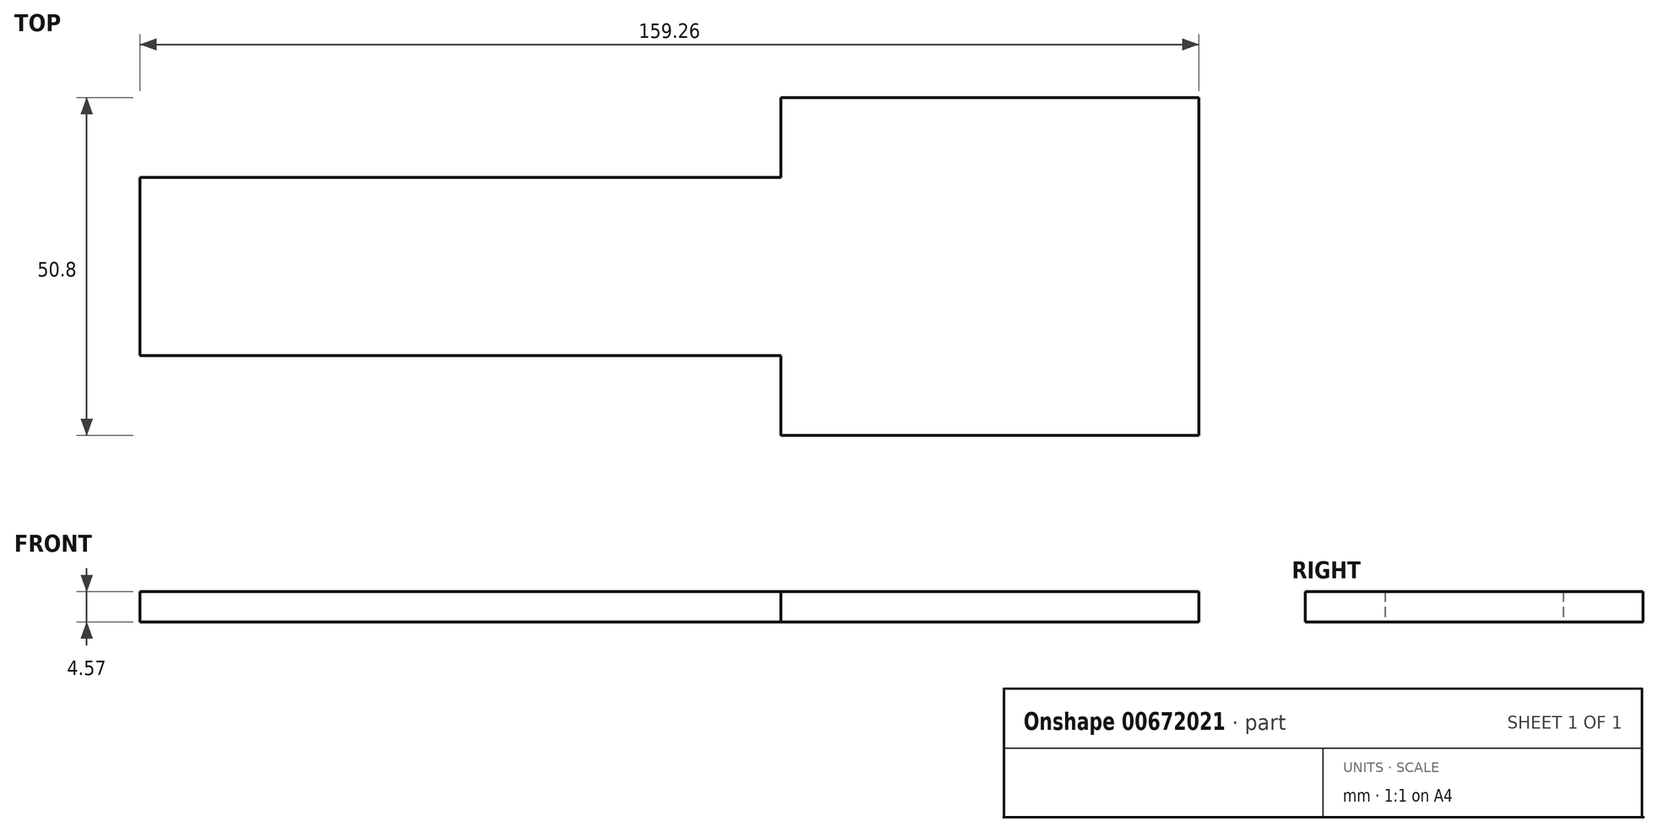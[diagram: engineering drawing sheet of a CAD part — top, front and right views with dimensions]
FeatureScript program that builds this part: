
annotation { "Feature Type Name" : "Feature", "Feature Type Description" : "" }
export const myFeature = defineFeature(function(context is Context, id is Id, definition is map)
    precondition{}
    {
        {
            var Q0;
            Q0=qCreatedBy(makeId("Top.planeOp"),FACE);
            var sketch = newSketch(context, id + "F0", { "sketchPlane" : qUnion([Q0])});
            skLineSegment(sketch, "E0", {"start": v(0, 0) * mm, "end": v(0, 25.4) * mm});
            skLineSegment(sketch, "E1", {"start": v(0, 25.4) * mm, "end": v(-62.87, 25.4) * mm});
            skLineSegment(sketch, "E2", {"start": v(-62.87, 25.4) * mm, "end": v(-62.87, 13.4) * mm});
            skLineSegment(sketch, "E3", {"start": v(-62.87, 13.4) * mm, "end": v(-159.26, 13.4) * mm});
            skLineSegment(sketch, "E4", {"start": v(-159.26, 13.4) * mm, "end": v(-159.26, 0) * mm});
            skLineSegment(sketch, "E5", {"start": v(-159.26, 0) * mm, "end": v(0, 0) * mm});
            skPoint(sketch, "E6", {"position": v(-73, 13.4) * mm});
            skSolve(sketch);
        }
        {
            var Q0;
            Q0 = qSketchRegion(id + "F0", true);
            extrude(context, id + "F1", {"entities" : qUnion([Q0]), "depth" : 4.57 * mm, "offsetDistance" : 25.4 * mm});
        }
        {
            var Q0;
            Q0=makeQuery(id+"F1.opExtrude","SWEPT_BODY",BODY,{"disambiguationData":[OSD([sQuery(id+"F0.wireOp",EDGE,"E0"),sQuery(id+"F0.wireOp",EDGE,"E1"),sQuery(id+"F0.wireOp",EDGE,"E2"),sQuery(id+"F0.wireOp",EDGE,"E3"),sQuery(id+"F0.wireOp",EDGE,"E4"),sQuery(id+"F0.wireOp",EDGE,"E5")])]});
            var Q1;
            Q1=makeQuery(id+"F1.opExtrude","SWEPT_FACE",FACE,{"disambiguationData":[OSD([sQuery(id+"F0.wireOp",EDGE,"E5")])]});
            mirror(context, id + "F2", {"operationType" : NewBodyOperationType.ADD, "entities" : qUnion([Q0]), "mirrorPlane" : qUnion([Q1])});
        }
    });
